FCSTD DOCUMENT  (FreeCAD 0.15R4671 (Git))
Label: test
License: All rights reserved
LicenseURL: http://en.wikipedia.org/wiki/All_rights_reserved
objects: Sketcher::SketchObject×1
note: 1 computed .brp shape members not serialized (recipe doc carries the construction recipe); baked Part::Feature solids carry a one-line shape summary decoded from their .brp

FEATURE [Sketcher::SketchObject] Sketch
  sketch-geometry (4):
    g0: LineSegment StartX=-52.7102 StartY=34.5524 StartZ=0 EndX=52.7692 EndY=34.5524 EndZ=0
    g1: LineSegment StartX=52.7692 StartY=34.5524 StartZ=0 EndX=52.7692 EndY=-35.9439 EndZ=0
    g2: LineSegment StartX=52.7692 StartY=-35.9439 StartZ=0 EndX=-52.7102 EndY=-35.9439 EndZ=0
    g3: LineSegment StartX=-52.7102 StartY=-35.9439 StartZ=0 EndX=-52.7102 EndY=34.5524 EndZ=0
  constraints (8):
    c: Coincident(g0,g1)
    c: Coincident(g1,g2)
    c: Coincident(g2,g3)
    c: Coincident(g3,g0)
    c: Horizontal(g0)
    c: Horizontal(g2)
    c: Vertical(g1)
    c: Vertical(g3)
